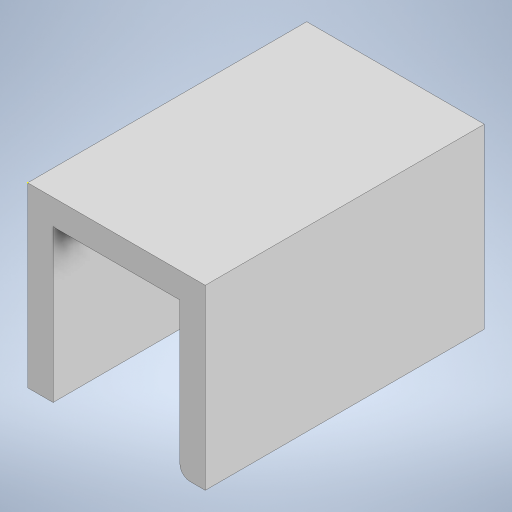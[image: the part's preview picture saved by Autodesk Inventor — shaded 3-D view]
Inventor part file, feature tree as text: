
AUTODESK INVENTOR PART (.ipt)
format: ipt  version: 2023 (Build 270158000, 158)  size: 210,432 bytes
history: native  units: in
note: dims shown in document units (in); Inventor stores cm internally (conversion verified against a paired STEP export)
features: sketch x9, extrude x4, fillet x1
ambient origin geometry x8: Origin, YZ Plane, XZ Plane, XY Plane, X Axis, Y Axis, Z Axis, Center Point
bodies: Solid1 (feature_tree)
feature tree (14):
  extrude  "Extrusion1"  Depth=0.5512in
  extrude  "Extrusion2"  Depth=0.3937in
  sketch  "Sketch8"  dims[d5=0.7874in d6=0.7874in d7=0.0in]
  sketch  "Sketch9"  dims[d30=0.1969in d31=0.4724in d32=0.0787in d33=0.0in]
  sketch  "Sketch11"  dims[d34=0.1772in]
  sketch  "Sketch14"  dims[d35=0.1378in]
  sketch  "Sketch15"  dims[d36=0.3543in d37=0.0in]
  extrude  "Extrusion10"  Depth=0.7874in TaperAngle=0.0deg
  extrude  "Extrusion11"  Depth=0.4724in
  fillet  "Fillet1"  Radius=0.0787in
  sketch  "Sketch1"  dims[d0=0.5512in d1=0.5512in]
  sketch  "Sketch2"  dims[d2=0.8661in d3=0.0in d4=0.3937in]
  sketch  "Sketch16"  dims[d38=0.0315in]
  sketch  "Sketch17"  dims[d39=0.0in d40=0.0in d41=0.0in]
